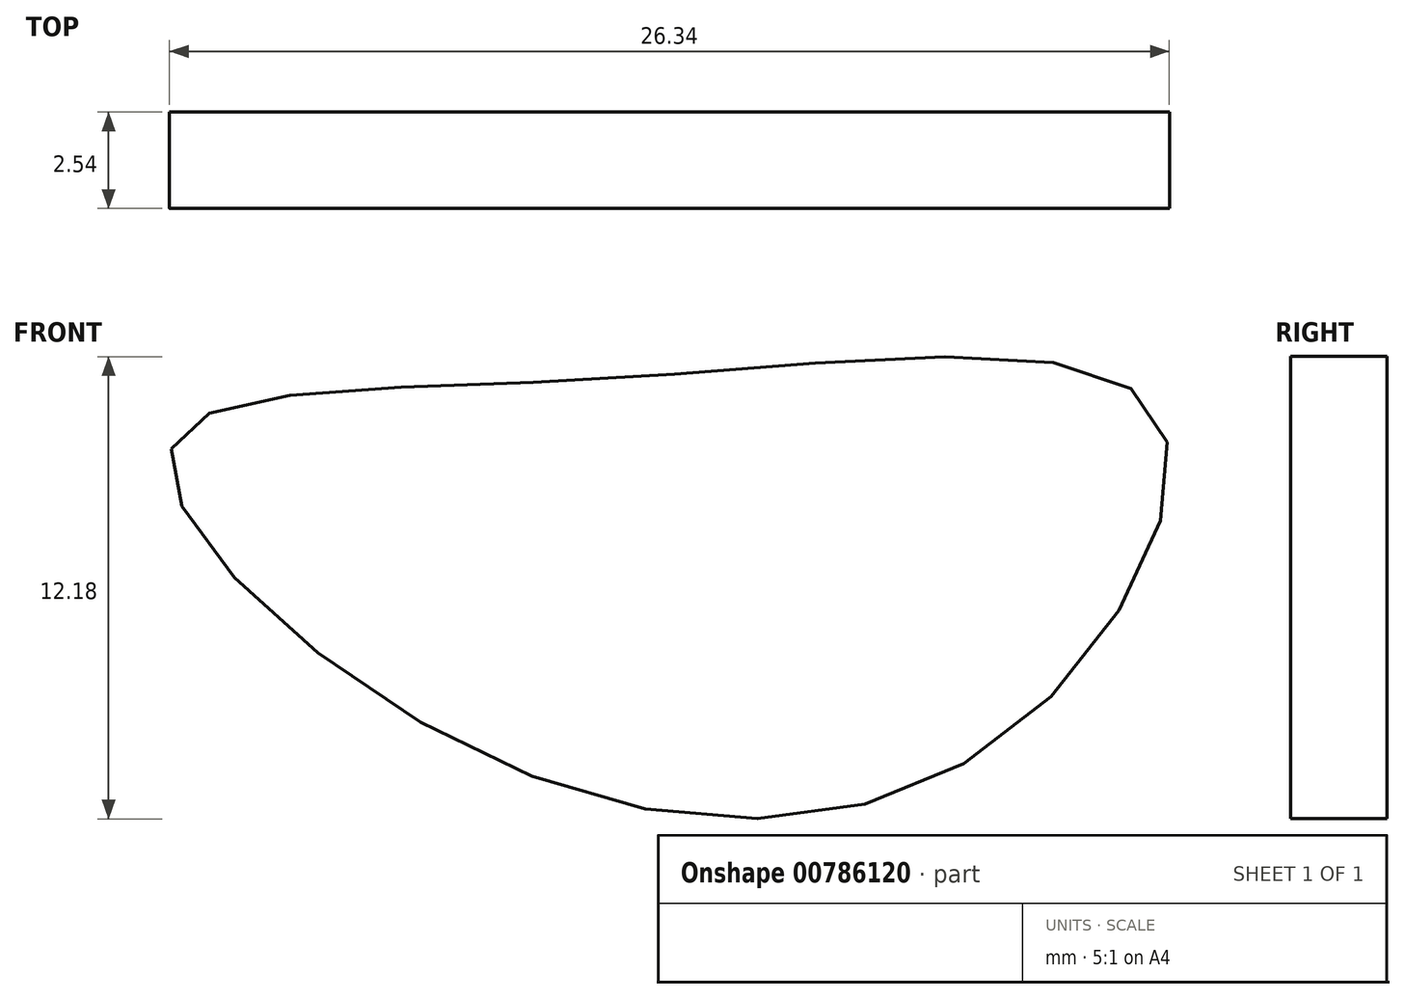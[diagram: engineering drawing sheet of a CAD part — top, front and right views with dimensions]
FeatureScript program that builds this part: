
annotation { "Feature Type Name" : "Feature", "Feature Type Description" : "" }
export const myFeature = defineFeature(function(context is Context, id is Id, definition is map)
    precondition{}
    {
        {
            var Q0;
            Q0=qCreatedBy(makeId("Front.planeOp"),FACE);
            var sketch = newSketch(context, id + "F0", { "sketchPlane" : qUnion([Q0])});
            skFitSpline(sketch, "E0", {"points": [v(-53.6, 7.79) * mm, v(-45.96, 0) * mm, v(-31.91, 0) * mm, v(-27.64, 8.7) * mm, v(-42.3, 9.62) * mm, v(-53.6, 7.79) * mm]});
            skSolve(sketch);
        }
        {
            var Q0;
            Q0=makeQuery(id+"F0.imprint","IMPRINT",FACE,{"disambiguationData":[TD([[makeQuery(id+"F0.imprint","IMPRINT",EDGE,{"derivedFrom":sQuery(id+"F0.wireOp",EDGE,"E0")}),1.0]])]});
            extrude(context, id + "F1", {"entities" : qUnion([Q0]), "depth" : 2.54 * mm, "offsetDistance" : 25.4 * mm});
        }
    });
